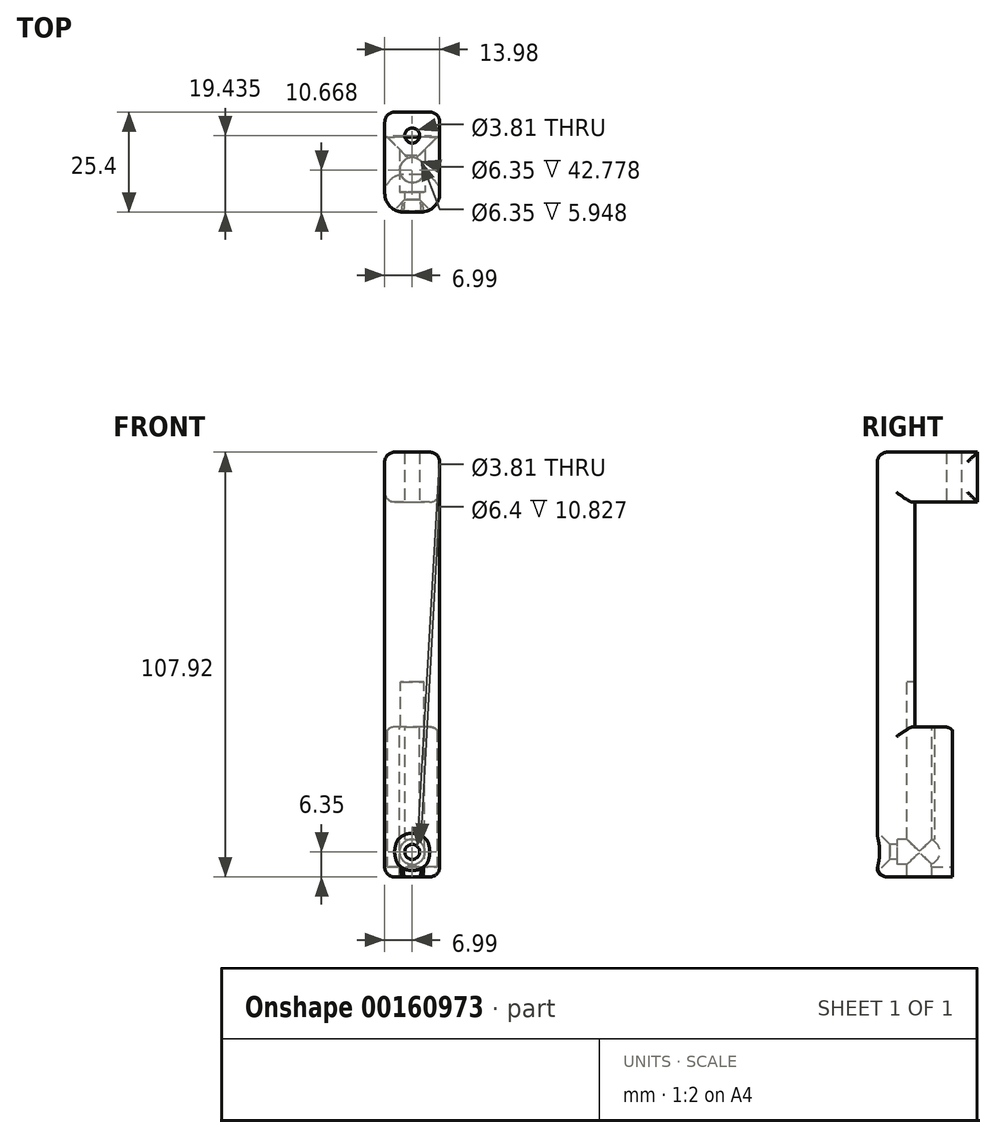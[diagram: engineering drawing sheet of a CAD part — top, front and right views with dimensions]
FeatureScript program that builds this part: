
annotation { "Feature Type Name" : "Feature", "Feature Type Description" : "" }
export const myFeature = defineFeature(function(context is Context, id is Id, definition is map)
    precondition{}
    {
        {
            var Q0;
            Q0=qCreatedBy(makeId("Top.planeOp"),FACE);
            var sketch = newSketch(context, id + "F0", { "sketchPlane" : qUnion([Q0])});
            skLineSegment(sketch, "E0", {"start": v(0, 0) * mm, "end": v(-6.35, 6.35) * mm});
            skLineSegment(sketch, "E1", {"start": v(-6.35, 6.35) * mm, "end": v(-6.99, 6.35) * mm});
            skLineSegment(sketch, "E2", {"start": v(-6.99, 6.35) * mm, "end": v(-6.99, -12.7) * mm});
            skLineSegment(sketch, "E3", {"start": v(-6.99, -12.7) * mm, "end": v(6.99, -12.7) * mm});
            skLineSegment(sketch, "E4", {"start": v(6.99, -12.7) * mm, "end": v(6.99, 6.35) * mm});
            skLineSegment(sketch, "E5", {"start": v(6.99, 6.35) * mm, "end": v(6.35, 6.35) * mm});
            skLineSegment(sketch, "E6", {"start": v(6.35, 6.35) * mm, "end": v(0, 0) * mm});
            skSolve(sketch);
        }
        {
            var Q0;
            Q0 = qSketchRegion(id + "F0", true);
            extrude(context, id + "F1", {"entities" : qUnion([Q0]), "depth" : 38.1 * mm});
        }
        {
            var Q0;
            Q0=makeQuery(id+"F1.opExtrude","CAP_FACE",FACE,{"disambiguationData":[OSD([sQuery(id+"F0.wireOp",EDGE,"E0"),sQuery(id+"F0.wireOp",EDGE,"E1"),sQuery(id+"F0.wireOp",EDGE,"E2"),sQuery(id+"F0.wireOp",EDGE,"E3"),sQuery(id+"F0.wireOp",EDGE,"E4"),sQuery(id+"F0.wireOp",EDGE,"E5"),sQuery(id+"F0.wireOp",EDGE,"E6")])],"isStart":true});
            var sketch = newSketch(context, id + "F2", { "sketchPlane" : qUnion([Q0])});
            skLineSegment(sketch, "E7.bottom", {"start": v(6.99, -6.35) * mm, "end": v(-6.99, -6.35) * mm});
            skLineSegment(sketch, "E7.top", {"start": v(6.99, 4.25) * mm, "end": v(-6.99, 4.25) * mm});
            skLineSegment(sketch, "E7.left", {"start": v(6.99, -6.35) * mm, "end": v(6.99, 4.25) * mm});
            skLineSegment(sketch, "E7.right", {"start": v(-6.99, -6.35) * mm, "end": v(-6.99, 4.25) * mm});
            skSolve(sketch);
        }
        {
            var Q0;
            Q0 = qSketchRegion(id + "F2", true);
            extrude(context, id + "F3", {"entities" : qUnion([Q0]), "operationType" : NewBodyOperationType.ADD, "oppositeDirection" : true, "depth" : 2.54 * mm});
        }
        {
            var Q0;
            Q0=makeQuery(id+"F1.opExtrude","SWEPT_FACE",FACE,{"disambiguationData":[OSD([sQuery(id+"F0.wireOp",EDGE,"E3")])]});
            var sketch = newSketch(context, id + "F4", { "sketchPlane" : qUnion([Q0])});
            skCircle(sketch, "E8", {"center": v(0, 6.35) * mm, "radius": 4.76 * mm});
            skSolve(sketch);
        }
        {
            var Q0;
            Q0 = qSketchRegion(id + "F4", true);
            extrude(context, id + "F5", {"entities" : qUnion([Q0]), "operationType" : NewBodyOperationType.REMOVE, "oppositeDirection" : true, "depth" : 0.25 * mm});
        }
        {
            var Q0;
            Q0=makeQuery(id+"F5.boolean.opBoolean","COPY",FACE,{"derivedFrom":makeQuery(id+"F5.opExtrude","CAP_FACE",FACE,{"disambiguationData":[OSD([sQuery(id+"F4.wireOp",EDGE,"E8")])],"isStart":false})});
            var sketch = newSketch(context, id + "F6", { "sketchPlane" : qUnion([Q0])});
            skCircle(sketch, "E9.0.0", {"center": v(0, 6.35) * mm, "radius": 4.76 * mm});
            skSolve(sketch);
        }
        {
            var Q0;
            Q0 = qSketchRegion(id + "F6", true);
            extrude(context, id + "F7", {"entities" : qUnion([Q0]), "operationType" : NewBodyOperationType.REMOVE, "oppositeDirection" : true, "depth" : 3.17 * mm, "hasDraft" : true, "draftAngle" : 45 * degree, "draftPullDirection" : true});
        }
        {
            var Q0;
            Q0=makeQuery(id+"F1.opExtrude","SWEPT_FACE",FACE,{"disambiguationData":[OSD([sQuery(id+"F0.wireOp",EDGE,"E3")])]});
            var sketch = newSketch(context, id + "F8", { "sketchPlane" : qUnion([Q0])});
            skCircle(sketch, "E10", {"center": v(0, 6.35) * mm, "radius": 1.9 * mm});
            skSolve(sketch);
        }
        {
            var Q0;
            Q0 = qSketchRegion(id + "F8", true);
            extrude(context, id + "F9", {"entities" : qUnion([Q0]), "operationType" : NewBodyOperationType.REMOVE, "oppositeDirection" : true, "depth" : 25.4 * mm});
        }
        {
            var Q0;
            Q0=makeQuery(id+"F1.opExtrude","SWEPT_FACE",FACE,{"disambiguationData":[OSD([sQuery(id+"F0.wireOp",EDGE,"E3")])]});
            var sketch = newSketch(context, id + "F10", { "sketchPlane" : qUnion([Q0])});
            skCircle(sketch, "E11", {"center": v(0, 6.35) * mm, "radius": 3.2 * mm});
            skSolve(sketch);
        }
        {
            var Q0;
            Q0 = qSketchRegion(id + "F10", true);
            extrude(context, id + "F11", {"entities" : qUnion([Q0]), "operationType" : NewBodyOperationType.REMOVE, "oppositeDirection" : true, "depth" : 25.4 * mm, "hasSecondDirection" : true, "secondDirectionOppositeDirection" : true, "secondDirectionDepth" : 5.08 * mm});
        }
        {
            var Q0;
            Q0=makeQuery(id+"F1.opExtrude","SWEPT_FACE",FACE,{"disambiguationData":[OSD([sQuery(id+"F0.wireOp",EDGE,"E4")])]});
            var sketch = newSketch(context, id + "F12", { "sketchPlane" : qUnion([Q0])});
            skLineSegment(sketch, "E12", {"start": v(-12.7, 38.1) * mm, "end": v(-12.7, 107.92) * mm});
            skLineSegment(sketch, "E13", {"start": v(-12.7, 107.92) * mm, "end": v(12.7, 107.92) * mm});
            skLineSegment(sketch, "E14", {"start": v(12.7, 107.92) * mm, "end": v(12.7, 95.22) * mm});
            skLineSegment(sketch, "E15", {"start": v(12.7, 95.22) * mm, "end": v(-3.18, 95.22) * mm});
            skLineSegment(sketch, "E16", {"start": v(-3.18, 95.22) * mm, "end": v(-3.17, 38.1) * mm});
            skLineSegment(sketch, "E17", {"start": v(-3.17, 38.1) * mm, "end": v(-12.7, 38.1) * mm});
            skSolve(sketch);
        }
        {
            var Q0;
            Q0 = qSketchRegion(id + "F12", true);
            extrude(context, id + "F13", {"entities" : qUnion([Q0]), "operationType" : NewBodyOperationType.ADD, "oppositeDirection" : true, "depth" : 13.97 * mm});
        }
        {
            var Q0;
            Q0=makeQuery(id+"F13.opExtrude","SWEPT_FACE",FACE,{"disambiguationData":[OSD([sQuery(id+"F12.wireOp",EDGE,"E15")])]});
            var sketch = newSketch(context, id + "F14", { "sketchPlane" : qUnion([Q0])});
            skCircle(sketch, "E18", {"center": v(0, -6.74) * mm, "radius": 4.76 * mm, "construction": true});
            skCircle(sketch, "E19", {"center": v(0, -6.74) * mm, "radius": 1.9 * mm});
            skSolve(sketch);
        }
        {
            var Q0;
            Q0 = qSketchRegion(id + "F14", true);
            extrude(context, id + "F15", {"entities" : qUnion([Q0]), "operationType" : NewBodyOperationType.REMOVE, "oppositeDirection" : true, "depth" : 25.4 * mm});
        }
        {
            var Q0;
            Q0=makeQuery(id+"F13.boolean.opBoolean","MERGE",EDGE,{"derivedFrom":[makeQuery(id+"F1.opExtrude","SWEPT_EDGE",EDGE,{"disambiguationData":[OSD([sQuery(id+"F0.wireOp",EDGE,"E3"),sQuery(id+"F0.wireOp",EDGE,"E4")])]}),makeQuery(id+"F13.opExtrude","CAP_EDGE",EDGE,{"disambiguationData":[OSD([sQuery(id+"F12.wireOp",EDGE,"E12")])],"isStart":true})]});
            var Q1;
            Q1=makeQuery(id+"F13.boolean.opBoolean","MERGE",EDGE,{"derivedFrom":[makeQuery(id+"F1.opExtrude","SWEPT_EDGE",EDGE,{"disambiguationData":[OSD([sQuery(id+"F0.wireOp",EDGE,"E2"),sQuery(id+"F0.wireOp",EDGE,"E3")])]}),makeQuery(id+"F13.opExtrude","CAP_EDGE",EDGE,{"disambiguationData":[OSD([sQuery(id+"F12.wireOp",EDGE,"E12")])],"isStart":false})]});
            var Q2;
            Q2=makeQuery(id+"F13.opExtrude","CAP_EDGE",EDGE,{"disambiguationData":[OSD([sQuery(id+"F12.wireOp",EDGE,"E16")])],"isStart":true});
            var Q3;
            Q3=makeQuery(id+"F13.opExtrude","CAP_EDGE",EDGE,{"disambiguationData":[OSD([sQuery(id+"F12.wireOp",EDGE,"E16")])],"isStart":false});
            fillet(context, id + "F16", {"entities" : qUnion([Q0, Q1, Q2, Q3]), "radius" : 4.76 * mm, "tangentPropagation" : true, "allowEdgeOverflow" : false});
        }
        {
            var Q0;
            Q0=makeQuery(id+"F13.opExtrude","CAP_EDGE",EDGE,{"disambiguationData":[OSD([sQuery(id+"F12.wireOp",EDGE,"E13")])],"isStart":true});
            var Q1;
            Q1=makeQuery(id+"F13.opExtrude","CAP_EDGE",EDGE,{"disambiguationData":[OSD([sQuery(id+"F12.wireOp",EDGE,"E13")])],"isStart":false});
            var Q2;
            Q2=makeQuery(id+"F1.opExtrude","CAP_EDGE",EDGE,{"disambiguationData":[OSD([sQuery(id+"F0.wireOp",EDGE,"E4")])],"isStart":true});
            var Q3;
            Q3=makeQuery(id+"F1.opExtrude","CAP_EDGE",EDGE,{"disambiguationData":[OSD([sQuery(id+"F0.wireOp",EDGE,"E2")])],"isStart":true});
            var Q4;
            Q4=makeQuery(id+"F1.opExtrude","CAP_EDGE",EDGE,{"disambiguationData":[OSD([sQuery(id+"F0.wireOp",EDGE,"E3")])],"isStart":true});
            var Q5;
            Q5=makeQuery(id+"F13.opExtrude","SWEPT_EDGE",EDGE,{"disambiguationData":[OSD([sQuery(id+"F12.wireOp",EDGE,"E12"),sQuery(id+"F12.wireOp",EDGE,"E13")])]});
            var Q6;
            Q6=makeQuery(id+"F13.opExtrude","CAP_EDGE",EDGE,{"disambiguationData":[OSD([sQuery(id+"F12.wireOp",EDGE,"E15")])],"isStart":true});
            var Q7;
            Q7=makeQuery(id+"F13.opExtrude","CAP_EDGE",EDGE,{"disambiguationData":[OSD([sQuery(id+"F12.wireOp",EDGE,"E14")])],"isStart":true});
            var Q8;
            Q8=makeQuery(id+"F13.opExtrude","CAP_EDGE",EDGE,{"disambiguationData":[OSD([sQuery(id+"F12.wireOp",EDGE,"E14")])],"isStart":false});
            var Q9;
            Q9=makeQuery(id+"F13.opExtrude","CAP_EDGE",EDGE,{"disambiguationData":[OSD([sQuery(id+"F12.wireOp",EDGE,"E15")])],"isStart":false});
            var Q10;
            Q10=makeQuery(id+"F1.opExtrude","CAP_EDGE",EDGE,{"disambiguationData":[OSD([sQuery(id+"F0.wireOp",EDGE,"E4")])],"isStart":false});
            var Q11;
            Q11=makeQuery(id+"F1.opExtrude","CAP_EDGE",EDGE,{"disambiguationData":[OSD([sQuery(id+"F0.wireOp",EDGE,"E2")])],"isStart":false});
            fillet(context, id + "F17", {"entities" : qUnion([Q0, Q1, Q2, Q3, Q4, Q5, Q6, Q7, Q8, Q9, Q10, Q11]), "radius" : 2.54 * mm, "tangentPropagation" : true, "allowEdgeOverflow" : false});
        }
        {
            var Q0;
            Q0=qCreatedBy(makeId("Front.planeOp"),FACE);
            var sketch = newSketch(context, id + "F18", { "sketchPlane" : qUnion([Q0])});
            skLineSegment(sketch, "E20.bottom", {"start": v(-4.46, 9.55) * mm, "end": v(4.45, 9.55) * mm});
            skLineSegment(sketch, "E20.top", {"start": v(-4.46, 38.1) * mm, "end": v(4.44, 38.1) * mm});
            skLineSegment(sketch, "E20.left", {"start": v(-4.46, 9.55) * mm, "end": v(-4.46, 38.1) * mm});
            skLineSegment(sketch, "E20.right", {"start": v(4.45, 9.55) * mm, "end": v(4.44, 38.1) * mm});
            skSolve(sketch);
        }
        {
            var Q0;
            Q0 = qSketchRegion(id + "F18", true);
            extrude(context, id + "F19", {"entities" : qUnion([Q0]), "operationType" : NewBodyOperationType.ADD, "oppositeDirection" : true, "depth" : 1.78 * mm});
        }
        {
            var Q0;
            Q0=makeQuery(id+"F19.boolean.opBoolean","MERGE",FACE,{"derivedFrom":[makeQuery(id+"F1.opExtrude","CAP_FACE",FACE,{"disambiguationData":[OSD([sQuery(id+"F0.wireOp",EDGE,"E0"),sQuery(id+"F0.wireOp",EDGE,"E1"),sQuery(id+"F0.wireOp",EDGE,"E2"),sQuery(id+"F0.wireOp",EDGE,"E3"),sQuery(id+"F0.wireOp",EDGE,"E4"),sQuery(id+"F0.wireOp",EDGE,"E5"),sQuery(id+"F0.wireOp",EDGE,"E6")])],"isStart":false}),makeQuery(id+"F19.opExtrude","SWEPT_FACE",FACE,{"disambiguationData":[OSD([sQuery(id+"F18.wireOp",EDGE,"E20.top")])]})]});
            var sketch = newSketch(context, id + "F20", { "sketchPlane" : qUnion([Q0])});
            skCircle(sketch, "E21", {"center": v(0, -2.03) * mm, "radius": 3.18 * mm});
            skSolve(sketch);
        }
        {
            var Q0;
            Q0 = qSketchRegion(id + "F20", true);
            extrude(context, id + "F21", {"entities" : qUnion([Q0]), "operationType" : NewBodyOperationType.REMOVE, "endBound" : BoundingType.THROUGH_ALL, "oppositeDirection" : true, "depth" : 27.94 * mm, "hasSecondDirection" : true, "secondDirectionOppositeDirection" : false, "secondDirectionDepth" : 11.43 * mm});
        }
    });
